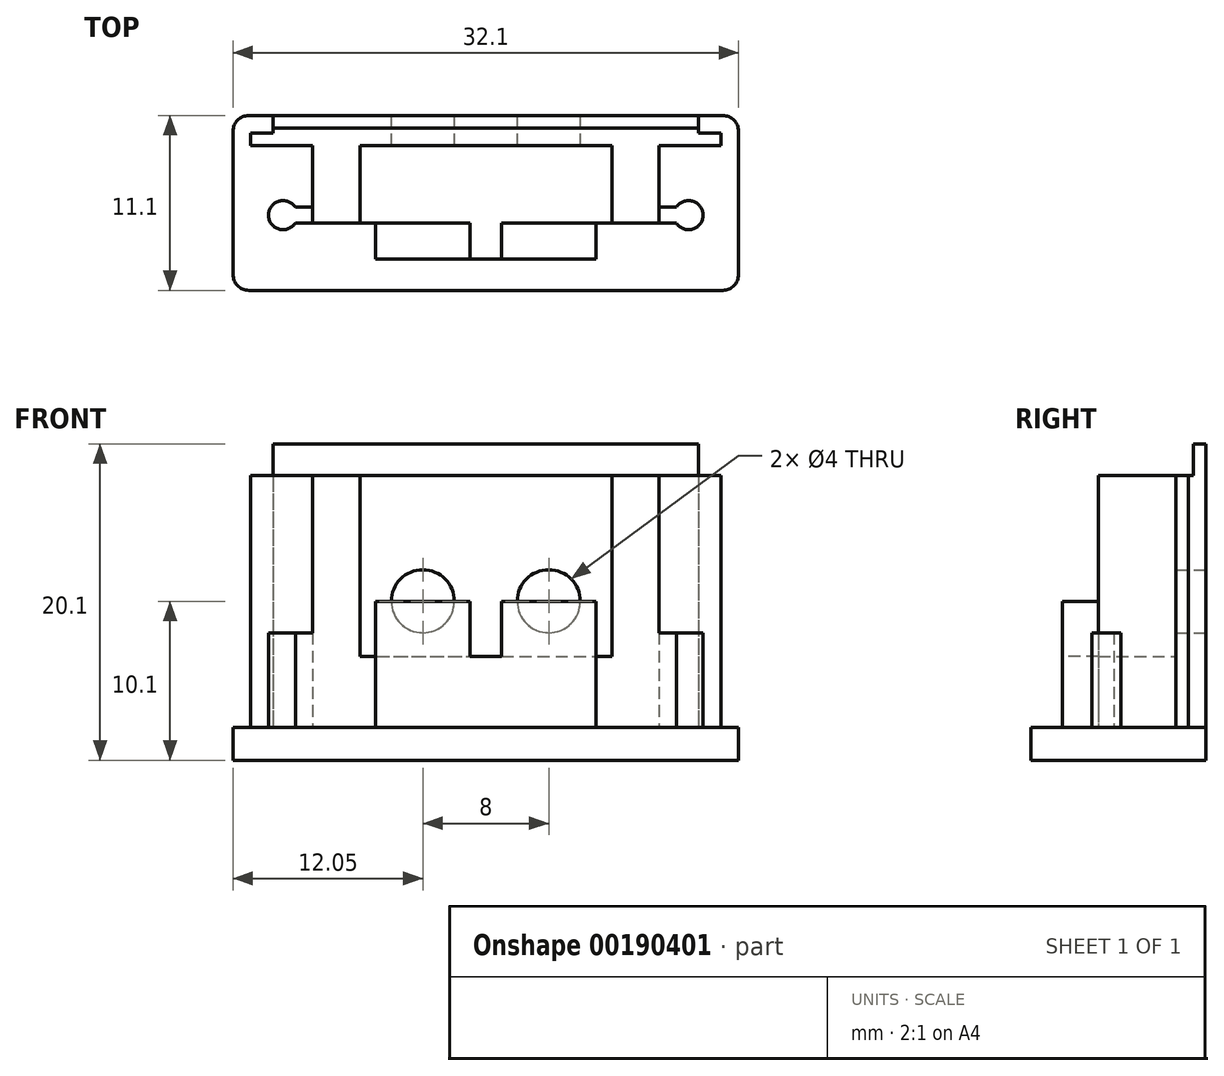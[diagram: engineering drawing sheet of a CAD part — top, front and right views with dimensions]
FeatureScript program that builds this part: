
annotation { "Feature Type Name" : "Feature", "Feature Type Description" : "" }
export const myFeature = defineFeature(function(context is Context, id is Id, definition is map)
    precondition{}
    {
        {
            var Q0;
            Q0=qCreatedBy(makeId("Top.planeOp"),FACE);
            var sketch = newSketch(context, id + "F0", { "sketchPlane" : qUnion([Q0])});
            skLineSegment(sketch, "E0.bottom", {"start": v(-15.05, 5.55) * mm, "end": v(15.05, 5.55) * mm});
            skLineSegment(sketch, "E0.top", {"start": v(-15.05, -5.55) * mm, "end": v(15.05, -5.55) * mm});
            skLineSegment(sketch, "E0.left", {"start": v(-16.05, 4.55) * mm, "end": v(-16.05, -4.55) * mm});
            skLineSegment(sketch, "E0.right", {"start": v(16.05, 4.55) * mm, "end": v(16.05, -4.55) * mm});
            skPoint(sketch, "E1.visualSharp", {"position": v(-16.05, 5.55) * mm});
            skArc(sketch, "E1.filletArc", {"start": v(-15.05, 5.55) * mm, "mid": v(-15.76, 5.26) * mm, "end": v(-16.05, 4.55) * mm});
            skPoint(sketch, "E2.visualSharp", {"position": v(-16.05, -5.55) * mm});
            skArc(sketch, "E2.filletArc", {"start": v(-16.05, -4.55) * mm, "mid": v(-15.76, -5.26) * mm, "end": v(-15.05, -5.55) * mm});
            skPoint(sketch, "E3.visualSharp", {"position": v(16.05, 5.55) * mm});
            skArc(sketch, "E3.filletArc", {"start": v(16.05, 4.55) * mm, "mid": v(15.76, 5.26) * mm, "end": v(15.05, 5.55) * mm});
            skPoint(sketch, "E4.visualSharp", {"position": v(16.05, -5.55) * mm});
            skArc(sketch, "E4.filletArc", {"start": v(15.05, -5.55) * mm, "mid": v(15.76, -5.26) * mm, "end": v(16.05, -4.55) * mm});
            skSolve(sketch);
        }
        {
            var Q0;
            Q0=makeQuery(id+"F0.imprint","IMPRINT",FACE,{"disambiguationData":[TD([[makeQuery(id+"F0.imprint","IMPRINT",EDGE,{"derivedFrom":sQuery(id+"F0.wireOp",EDGE,"E0.bottom")}),-1.0]])]});
            extrude(context, id + "F1", {"entities" : qUnion([Q0]), "depth" : 2.1 * mm});
        }
        {
            var Q0;
            Q0=makeQuery(id+"F1.opExtrude","CAP_FACE",FACE,{"disambiguationData":[OSD([sQuery(id+"F0.wireOp",EDGE,"E0.bottom"),sQuery(id+"F0.wireOp",EDGE,"E0.top"),sQuery(id+"F0.wireOp",EDGE,"E0.left"),sQuery(id+"F0.wireOp",EDGE,"E0.right"),sQuery(id+"F0.wireOp",EDGE,"E1.filletArc"),sQuery(id+"F0.wireOp",EDGE,"E2.filletArc"),sQuery(id+"F0.wireOp",EDGE,"E3.filletArc"),sQuery(id+"F0.wireOp",EDGE,"E4.filletArc")])],"isStart":false});
            var sketch = newSketch(context, id + "F2", { "sketchPlane" : qUnion([Q0])});
            skLineSegment(sketch, "E5.bottom", {"start": v(-13.5, 5.55) * mm, "end": v(13.5, 5.55) * mm});
            skLineSegment(sketch, "E5.top", {"start": v(-13.5, 4.45) * mm, "end": v(13.5, 4.45) * mm});
            skLineSegment(sketch, "E5.left", {"start": v(-13.5, 5.55) * mm, "end": v(-13.5, 4.45) * mm});
            skLineSegment(sketch, "E5.right", {"start": v(13.5, 5.55) * mm, "end": v(13.5, 4.45) * mm});
            skLineSegment(sketch, "E6.bottom", {"start": v(-14.93, 4.45) * mm, "end": v(14.93, 4.45) * mm});
            skLineSegment(sketch, "E6.top", {"start": v(-14.93, 3.65) * mm, "end": v(14.93, 3.65) * mm});
            skLineSegment(sketch, "E6.left", {"start": v(-14.93, 4.45) * mm, "end": v(-14.93, 3.65) * mm});
            skLineSegment(sketch, "E6.right", {"start": v(14.93, 4.45) * mm, "end": v(14.93, 3.65) * mm});
            skCircle(sketch, "E7", {"center": v(-12.88, -0.77) * mm, "radius": 0.93 * mm});
            skCircle(sketch, "E8", {"center": v(12.88, -0.78) * mm, "radius": 0.93 * mm});
            skLineSegment(sketch, "E9.bottom", {"start": v(-12.88, -0.27) * mm, "end": v(12.88, -0.28) * mm});
            skLineSegment(sketch, "E9.top", {"start": v(-12.88, -1.27) * mm, "end": v(12.88, -1.28) * mm});
            skLineSegment(sketch, "E9.left", {"start": v(-12.88, -0.27) * mm, "end": v(-12.88, -1.27) * mm});
            skLineSegment(sketch, "E9.right", {"start": v(12.88, -0.28) * mm, "end": v(12.88, -1.28) * mm});
            skLineSegment(sketch, "E10", {"start": v(-12.88, -0.77) * mm, "end": v(12.88, -0.78) * mm, "construction": true});
            skSolve(sketch);
        }
        {
            var Q0;
            {var subQ5=sQuery(id+"F2.wireOp",EDGE,"E9.right");Q0=makeQuery(id+"F2.imprint","IMPRINT",FACE,{"disambiguationData":[TD([[makeQuery(id+"F2.imprint","IMPRINT",EDGE,{"derivedFrom":subQ5}),1.0]])]});}
            var Q1;
            {var subQ0=sQuery(id+"F2.wireOp",EDGE,"E9.bottom");var subQ1=sQuery(id+"F2.wireOp",EDGE,"E7");var subQ2=makeQuery(id+"F2.imprint","INTERSECT",VERTEX,{"derivedFrom":[subQ1,subQ0]});Q1=makeQuery(id+"F2.imprint","IMPRINT",FACE,{"disambiguationData":[TD([[makeQuery(id+"F2.imprint","IMPRINT",EDGE,{"disambiguationData":[TD([[subQ2,1.0]])],"derivedFrom":subQ1}),-1.0]])]});}
            var Q2;
            {var subQ5=sQuery(id+"F2.wireOp",EDGE,"E9.right");Q2=makeQuery(id+"F2.imprint","IMPRINT",FACE,{"disambiguationData":[TD([[makeQuery(id+"F2.imprint","IMPRINT",EDGE,{"derivedFrom":subQ5}),-1.0]])]});}
            var Q3;
            {var subQ5=sQuery(id+"F2.wireOp",EDGE,"E9.left");Q3=makeQuery(id+"F2.imprint","IMPRINT",FACE,{"disambiguationData":[TD([[makeQuery(id+"F2.imprint","IMPRINT",EDGE,{"derivedFrom":subQ5}),-1.0]])]});}
            var Q4;
            {var subQ5=sQuery(id+"F2.wireOp",EDGE,"E9.left");Q4=makeQuery(id+"F2.imprint","IMPRINT",FACE,{"disambiguationData":[TD([[makeQuery(id+"F2.imprint","IMPRINT",EDGE,{"derivedFrom":subQ5}),1.0]])]});}
            var Q5;
            Q5=makeQuery(id+"F2.imprint","IMPRINT",FACE,{"disambiguationData":[TD([[makeQuery(id+"F2.imprint","IMPRINT",EDGE,{"derivedFrom":sQuery(id+"F2.wireOp",EDGE,"E6.top")}),1.0]])]});
            var Q6;
            Q6=makeQuery(id+"F2.imprint","IMPRINT",FACE,{"disambiguationData":[TD([[makeQuery(id+"F2.imprint","IMPRINT",EDGE,{"derivedFrom":sQuery(id+"F2.wireOp",EDGE,"E5.bottom")}),-1.0]])]});
            extrude(context, id + "F3", {"entities" : qUnion([Q0, Q1, Q2, Q3, Q4, Q5, Q6]), "operationType" : NewBodyOperationType.ADD, "depth" : 4.5 * mm});
        }
        {
            var Q0;
            Q0=makeQuery(id+"F3.opExtrude","CAP_FACE",FACE,{"disambiguationData":[OSD([sQuery(id+"F2.wireOp",EDGE,"E5.bottom"),sQuery(id+"F2.wireOp",EDGE,"E5.left"),sQuery(id+"F2.wireOp",EDGE,"E5.right"),sQuery(id+"F2.wireOp",EDGE,"E6.bottom"),sQuery(id+"F2.wireOp",EDGE,"E6.top"),sQuery(id+"F2.wireOp",EDGE,"E6.left"),sQuery(id+"F2.wireOp",EDGE,"E6.right")])],"isStart":false});
            extrude(context, id + "F4", {"entities" : qUnion([Q0]), "operationType" : NewBodyOperationType.ADD, "depth" : (10 + 1.5) * mm});
        }
        {
            var Q0;
            {var subQ0=sQuery(id+"F2.wireOp",EDGE,"E5.bottom");Q0=makeQuery(id+"F4.boolean.opBoolean","MERGE",FACE,{"derivedFrom":[makeQuery(id+"F3.boolean.opBoolean","MERGE",FACE,{"derivedFrom":[makeQuery(id+"F1.opExtrude","SWEPT_FACE",FACE,{"disambiguationData":[OSD([sQuery(id+"F0.wireOp",EDGE,"E0.bottom")])]}),makeQuery(id+"F3.opExtrude","SWEPT_FACE",FACE,{"disambiguationData":[OSD([subQ0])]})]}),makeQuery(id+"F4.opExtrude","SWEPT_FACE",FACE,{"disambiguationData":[OSD([subQ0])]})]});}
            var sketch = newSketch(context, id + "F5", { "sketchPlane" : qUnion([Q0])});
            skCircle(sketch, "E11", {"center": v(-4, 10.1) * mm, "radius": 2 * mm});
            skCircle(sketch, "E12", {"center": v(4, 10.1) * mm, "radius": 2 * mm});
            skSolve(sketch);
        }
        {
            var Q0;
            Q0=makeQuery(id+"F5.imprint","IMPRINT",FACE,{"disambiguationData":[TD([[makeQuery(id+"F5.imprint","IMPRINT",EDGE,{"derivedFrom":sQuery(id+"F5.wireOp",EDGE,"E12")}),1.0]])]});
            var Q1;
            Q1=makeQuery(id+"F5.imprint","IMPRINT",FACE,{"disambiguationData":[TD([[makeQuery(id+"F5.imprint","IMPRINT",EDGE,{"derivedFrom":sQuery(id+"F5.wireOp",EDGE,"E11")}),1.0]])]});
            extrude(context, id + "F6", {"entities" : qUnion([Q0, Q1]), "operationType" : NewBodyOperationType.REMOVE, "oppositeDirection" : true, "depth" : 25 * mm});
        }
        {
            var Q0;
            Q0=makeQuery(id+"F1.opExtrude","CAP_FACE",FACE,{"disambiguationData":[OSD([sQuery(id+"F0.wireOp",EDGE,"E0.bottom"),sQuery(id+"F0.wireOp",EDGE,"E0.top"),sQuery(id+"F0.wireOp",EDGE,"E0.left"),sQuery(id+"F0.wireOp",EDGE,"E0.right"),sQuery(id+"F0.wireOp",EDGE,"E1.filletArc"),sQuery(id+"F0.wireOp",EDGE,"E2.filletArc"),sQuery(id+"F0.wireOp",EDGE,"E3.filletArc"),sQuery(id+"F0.wireOp",EDGE,"E4.filletArc")])],"isStart":false});
            var sketch = newSketch(context, id + "F7", { "sketchPlane" : qUnion([Q0])});
            skLineSegment(sketch, "E13.bottom", {"start": v(-11, -0.27) * mm, "end": v(11, -0.27) * mm});
            skLineSegment(sketch, "E13.top", {"start": v(-11, 3.65) * mm, "end": v(11, 3.65) * mm});
            skLineSegment(sketch, "E13.left", {"start": v(-11, -0.28) * mm, "end": v(-11, 3.65) * mm});
            skLineSegment(sketch, "E13.right", {"start": v(11, -0.28) * mm, "end": v(11, 3.65) * mm});
            skSolve(sketch);
        }
        {
            var Q0;
            Q0=makeQuery(id+"F7.imprint","IMPRINT",FACE,{"disambiguationData":[TD([[makeQuery(id+"F7.imprint","IMPRINT",EDGE,{"derivedFrom":sQuery(id+"F7.wireOp",EDGE,"E13.bottom")}),1.0]])]});
            var Q1;
            Q1=makeQuery(id+"F3.opExtrude","CAP_FACE",FACE,{"disambiguationData":[OSD([sQuery(id+"F2.wireOp",EDGE,"E7"),sQuery(id+"F2.wireOp",EDGE,"E8"),sQuery(id+"F2.wireOp",EDGE,"E9.bottom"),sQuery(id+"F2.wireOp",EDGE,"E9.top")])],"isStart":false});
            extrude(context, id + "F8", {"entities" : qUnion([Q0]), "operationType" : NewBodyOperationType.ADD, "endBound" : BoundingType.UP_TO_SURFACE, "endBoundEntityFace" : qUnion([Q1]), "depth" : 25 * mm});
        }
        {
            var Q0;
            Q0=makeQuery(id+"F8.boolean.opBoolean","MERGE",FACE,{"derivedFrom":[makeQuery(id+"F3.opExtrude","CAP_FACE",FACE,{"disambiguationData":[OSD([sQuery(id+"F2.wireOp",EDGE,"E7"),sQuery(id+"F2.wireOp",EDGE,"E8"),sQuery(id+"F2.wireOp",EDGE,"E9.bottom"),sQuery(id+"F2.wireOp",EDGE,"E9.top")])],"isStart":false}),makeQuery(id+"F8.opExtrude","CAP_FACE",FACE,{"disambiguationData":[OSD([sQuery(id+"F7.wireOp",EDGE,"E13.bottom"),sQuery(id+"F7.wireOp",EDGE,"E13.top"),sQuery(id+"F7.wireOp",EDGE,"E13.left"),sQuery(id+"F7.wireOp",EDGE,"E13.right")])],"isStart":false})]});
            var sketch = newSketch(context, id + "F9", { "sketchPlane" : qUnion([Q0])});
            skArc(sketch, "E14.0.0", {"start": v(-12.1, -0.27) * mm, "mid": v(-13.8, -0.77) * mm, "end": v(-12.1, -1.27) * mm});
            skLineSegment(sketch, "E14.0.1", {"start": v(-12.1, -1.27) * mm, "end": v(12.1, -1.28) * mm});
            skArc(sketch, "E14.0.2", {"start": v(12.1, -1.28) * mm, "mid": v(13.8, -0.78) * mm, "end": v(12.1, -0.28) * mm});
            skLineSegment(sketch, "E14.0.3", {"start": v(12.1, -0.28) * mm, "end": v(11, -0.28) * mm});
            skLineSegment(sketch, "E14.0.4", {"start": v(11, -0.28) * mm, "end": v(11, 3.65) * mm});
            skLineSegment(sketch, "E14.0.5", {"start": v(11, 3.65) * mm, "end": v(-11, 3.65) * mm});
            skLineSegment(sketch, "E14.0.6", {"start": v(-11, 3.65) * mm, "end": v(-11, -0.27) * mm});
            skLineSegment(sketch, "E14.0.7", {"start": v(-11, -0.27) * mm, "end": v(-12.1, -0.27) * mm});
            skLineSegment(sketch, "E15", {"start": v(-8, -1.28) * mm, "end": v(-8, 3.65) * mm});
            skLineSegment(sketch, "E16", {"start": v(8, -1.28) * mm, "end": v(8, 3.65) * mm});
            skSolve(sketch);
        }
        {
            var Q0;
            {var subQ4=sQuery(id+"F9.wireOp",EDGE,"E14.0.0");Q0=makeQuery(id+"F9.imprint","IMPRINT",FACE,{"disambiguationData":[TD([[makeQuery(id+"F9.imprint","IMPRINT",EDGE,{"derivedFrom":subQ4}),1.0]])]});}
            var Q1;
            {var subQ1=sQuery(id+"F9.wireOp",EDGE,"E14.0.2");Q1=makeQuery(id+"F9.imprint","IMPRINT",FACE,{"disambiguationData":[TD([[makeQuery(id+"F9.imprint","IMPRINT",EDGE,{"derivedFrom":subQ1}),1.0]])]});}
            var Q2;
            Q2=makeQuery(id+"F4.opExtrude","CAP_FACE",FACE,{"disambiguationData":[OSD([sQuery(id+"F2.wireOp",EDGE,"E5.bottom"),sQuery(id+"F2.wireOp",EDGE,"E5.left"),sQuery(id+"F2.wireOp",EDGE,"E5.right"),sQuery(id+"F2.wireOp",EDGE,"E6.bottom"),sQuery(id+"F2.wireOp",EDGE,"E6.top"),sQuery(id+"F2.wireOp",EDGE,"E6.left"),sQuery(id+"F2.wireOp",EDGE,"E6.right")])],"isStart":false});
            extrude(context, id + "F10", {"entities" : qUnion([Q0, Q1]), "operationType" : NewBodyOperationType.ADD, "endBound" : BoundingType.UP_TO_SURFACE, "endBoundEntityFace" : qUnion([Q2]), "depth" : 25 * mm});
        }
        {
            var Q0;
            Q0=makeQuery(id+"F1.opExtrude","CAP_FACE",FACE,{"disambiguationData":[OSD([sQuery(id+"F0.wireOp",EDGE,"E0.bottom"),sQuery(id+"F0.wireOp",EDGE,"E0.top"),sQuery(id+"F0.wireOp",EDGE,"E0.left"),sQuery(id+"F0.wireOp",EDGE,"E0.right"),sQuery(id+"F0.wireOp",EDGE,"E1.filletArc"),sQuery(id+"F0.wireOp",EDGE,"E2.filletArc"),sQuery(id+"F0.wireOp",EDGE,"E3.filletArc"),sQuery(id+"F0.wireOp",EDGE,"E4.filletArc")])],"isStart":false});
            var sketch = newSketch(context, id + "F11", { "sketchPlane" : qUnion([Q0])});
            skLineSegment(sketch, "E17.bottom", {"start": v(-7, -1.28) * mm, "end": v(-1, -1.28) * mm});
            skLineSegment(sketch, "E17.top", {"start": v(-7, -3.55) * mm, "end": v(-1, -3.55) * mm});
            skLineSegment(sketch, "E17.left", {"start": v(-7, -1.28) * mm, "end": v(-7, -3.55) * mm});
            skLineSegment(sketch, "E17.right", {"start": v(-1, -1.28) * mm, "end": v(-1, -3.55) * mm});
            skLineSegment(sketch, "E18.MirrorCS", {"start": v(1, -1.28) * mm, "end": v(1, -3.55) * mm});
            skLineSegment(sketch, "E19.MirrorCS", {"start": v(7, -3.55) * mm, "end": v(1, -3.55) * mm});
            skLineSegment(sketch, "E20.MirrorCS", {"start": v(7, -1.28) * mm, "end": v(7, -3.55) * mm});
            skLineSegment(sketch, "E21.MirrorCS", {"start": v(7, -1.28) * mm, "end": v(1, -1.28) * mm});
            skSolve(sketch);
        }
        {
            var Q0;
            Q0=makeQuery(id+"F11.imprint","IMPRINT",FACE,{"disambiguationData":[TD([[makeQuery(id+"F11.imprint","IMPRINT",EDGE,{"derivedFrom":sQuery(id+"F11.wireOp",EDGE,"E17.bottom")}),-1.0]])]});
            var Q1;
            Q1=makeQuery(id+"F11.imprint","IMPRINT",FACE,{"disambiguationData":[TD([[makeQuery(id+"F11.imprint","IMPRINT",EDGE,{"derivedFrom":sQuery(id+"F11.wireOp",EDGE,"E18.MirrorCS")}),1.0]])]});
            extrude(context, id + "F12", {"entities" : qUnion([Q0, Q1]), "operationType" : NewBodyOperationType.ADD, "depth" : 8 * mm});
        }
        {
            var Q0;
            {var subQ0=sQuery(id+"F9.wireOp",EDGE,"E14.0.5");var subQ1=sQuery(id+"F9.wireOp",EDGE,"E14.0.1");Q0=makeQuery(id+"F10.boolean.opBoolean","MERGE",FACE,{"derivedFrom":[makeQuery(id+"F4.opExtrude","CAP_FACE",FACE,{"disambiguationData":[OSD([sQuery(id+"F2.wireOp",EDGE,"E5.bottom"),sQuery(id+"F2.wireOp",EDGE,"E5.left"),sQuery(id+"F2.wireOp",EDGE,"E5.right"),sQuery(id+"F2.wireOp",EDGE,"E6.bottom"),sQuery(id+"F2.wireOp",EDGE,"E6.top"),sQuery(id+"F2.wireOp",EDGE,"E6.left"),sQuery(id+"F2.wireOp",EDGE,"E6.right")])],"isStart":false}),makeQuery(id+"F10.opExtrude","CAP_FACE",FACE,{"disambiguationData":[OSD([sQuery(id+"F9.wireOp",EDGE,"E14.0.0"),subQ1,subQ0,sQuery(id+"F9.wireOp",EDGE,"E14.0.6"),sQuery(id+"F9.wireOp",EDGE,"E14.0.7"),sQuery(id+"F9.wireOp",EDGE,"E15")])],"isStart":false}),makeQuery(id+"F10.opExtrude","CAP_FACE",FACE,{"disambiguationData":[OSD([subQ1,sQuery(id+"F9.wireOp",EDGE,"E14.0.2"),sQuery(id+"F9.wireOp",EDGE,"E14.0.3"),sQuery(id+"F9.wireOp",EDGE,"E14.0.4"),subQ0,sQuery(id+"F9.wireOp",EDGE,"E16")])],"isStart":false})]});}
            var sketch = newSketch(context, id + "F13", { "sketchPlane" : qUnion([Q0])});
            skLineSegment(sketch, "E22.bottom", {"start": v(-13.5, 5.55) * mm, "end": v(13.5, 5.55) * mm});
            skLineSegment(sketch, "E22.left", {"start": v(-13.5, 5.55) * mm, "end": v(-13.5, 4.75) * mm});
            skLineSegment(sketch, "E22.right", {"start": v(13.5, 5.55) * mm, "end": v(13.5, 4.75) * mm});
            skLineSegment(sketch, "E23", {"start": v(-13.5, 4.75) * mm, "end": v(13.5, 4.75) * mm});
            skSolve(sketch);
        }
        {
            var Q0;
            Q0=makeQuery(id+"F13.imprint","IMPRINT",FACE,{"disambiguationData":[TD([[makeQuery(id+"F13.imprint","IMPRINT",EDGE,{"derivedFrom":sQuery(id+"F13.wireOp",EDGE,"E22.bottom")}),-1.0]])]});
            extrude(context, id + "F14", {"entities" : qUnion([Q0]), "operationType" : NewBodyOperationType.ADD, "depth" : 2 * mm});
        }
        {
            var Q0;
            Q0=makeQuery(id+"F1.opExtrude","CAP_FACE",FACE,{"disambiguationData":[OSD([sQuery(id+"F0.wireOp",EDGE,"E0.bottom"),sQuery(id+"F0.wireOp",EDGE,"E0.top"),sQuery(id+"F0.wireOp",EDGE,"E0.left"),sQuery(id+"F0.wireOp",EDGE,"E0.right"),sQuery(id+"F0.wireOp",EDGE,"E1.filletArc"),sQuery(id+"F0.wireOp",EDGE,"E2.filletArc"),sQuery(id+"F0.wireOp",EDGE,"E3.filletArc"),sQuery(id+"F0.wireOp",EDGE,"E4.filletArc")])],"isStart":false});
            var sketch = newSketch(context, id + "F15", { "sketchPlane" : qUnion([Q0])});
            skLineSegment(sketch, "E24.bottom", {"start": v(-1, -1.28) * mm, "end": v(1, -1.28) * mm});
            skLineSegment(sketch, "E24.top", {"start": v(-1, -3.55) * mm, "end": v(1, -3.55) * mm});
            skLineSegment(sketch, "E24.left", {"start": v(-1, -1.28) * mm, "end": v(-1, -3.55) * mm});
            skLineSegment(sketch, "E24.right", {"start": v(1, -1.28) * mm, "end": v(1, -3.55) * mm});
            skSolve(sketch);
        }
        {
            var Q0;
            Q0=makeQuery(id+"F15.imprint","IMPRINT",FACE,{"disambiguationData":[TD([[makeQuery(id+"F15.imprint","IMPRINT",EDGE,{"derivedFrom":sQuery(id+"F15.wireOp",EDGE,"E24.bottom")}),-1.0]])]});
            var Q1;
            Q1=makeQuery(id+"F8.boolean.opBoolean","MERGE",FACE,{"derivedFrom":[makeQuery(id+"F3.opExtrude","CAP_FACE",FACE,{"disambiguationData":[OSD([sQuery(id+"F2.wireOp",EDGE,"E7"),sQuery(id+"F2.wireOp",EDGE,"E8"),sQuery(id+"F2.wireOp",EDGE,"E9.bottom"),sQuery(id+"F2.wireOp",EDGE,"E9.top")])],"isStart":false}),makeQuery(id+"F8.opExtrude","CAP_FACE",FACE,{"disambiguationData":[OSD([sQuery(id+"F7.wireOp",EDGE,"E13.bottom"),sQuery(id+"F7.wireOp",EDGE,"E13.top"),sQuery(id+"F7.wireOp",EDGE,"E13.left"),sQuery(id+"F7.wireOp",EDGE,"E13.right")])],"isStart":false})]});
            extrude(context, id + "F16", {"entities" : qUnion([Q0]), "operationType" : NewBodyOperationType.ADD, "endBound" : BoundingType.UP_TO_SURFACE, "endBoundEntityFace" : qUnion([Q1]), "depth" : 25 * mm});
        }
        {
            var Q0;
            {var subQ0=sQuery(id+"F9.wireOp",EDGE,"E14.0.5");var subQ1=sQuery(id+"F9.wireOp",EDGE,"E14.0.1");Q0=makeQuery(id+"F10.boolean.opBoolean","MERGE",FACE,{"derivedFrom":[makeQuery(id+"F4.opExtrude","CAP_FACE",FACE,{"disambiguationData":[OSD([sQuery(id+"F2.wireOp",EDGE,"E5.bottom"),sQuery(id+"F2.wireOp",EDGE,"E5.left"),sQuery(id+"F2.wireOp",EDGE,"E5.right"),sQuery(id+"F2.wireOp",EDGE,"E6.bottom"),sQuery(id+"F2.wireOp",EDGE,"E6.top"),sQuery(id+"F2.wireOp",EDGE,"E6.left"),sQuery(id+"F2.wireOp",EDGE,"E6.right")])],"isStart":false}),makeQuery(id+"F10.opExtrude","CAP_FACE",FACE,{"disambiguationData":[OSD([sQuery(id+"F9.wireOp",EDGE,"E14.0.0"),subQ1,subQ0,sQuery(id+"F9.wireOp",EDGE,"E14.0.6"),sQuery(id+"F9.wireOp",EDGE,"E14.0.7"),sQuery(id+"F9.wireOp",EDGE,"E15")])],"isStart":false}),makeQuery(id+"F10.opExtrude","CAP_FACE",FACE,{"disambiguationData":[OSD([subQ1,sQuery(id+"F9.wireOp",EDGE,"E14.0.2"),sQuery(id+"F9.wireOp",EDGE,"E14.0.3"),sQuery(id+"F9.wireOp",EDGE,"E14.0.4"),subQ0,sQuery(id+"F9.wireOp",EDGE,"E16")])],"isStart":false})]});}
            var sketch = newSketch(context, id + "F17", { "sketchPlane" : qUnion([Q0])});
            skLineSegment(sketch, "E25.0.0", {"start": v(13.5, 4.75) * mm, "end": v(-13.5, 4.75) * mm});
            skLineSegment(sketch, "E25.0.1", {"start": v(-13.5, 4.75) * mm, "end": v(-13.5, 4.45) * mm});
            skLineSegment(sketch, "E25.0.2", {"start": v(-13.5, 4.45) * mm, "end": v(-14.93, 4.45) * mm});
            skLineSegment(sketch, "E25.0.3", {"start": v(-14.93, 4.45) * mm, "end": v(-14.93, 3.65) * mm});
            skLineSegment(sketch, "E25.0.4", {"start": v(-14.93, 3.65) * mm, "end": v(-11, 3.65) * mm});
            skLineSegment(sketch, "E25.0.5", {"start": v(-11, 3.65) * mm, "end": v(-11, -0.27) * mm});
            skLineSegment(sketch, "E25.0.6", {"start": v(-11, -0.27) * mm, "end": v(-12.1, -0.27) * mm});
            skArc(sketch, "E25.0.7", {"start": v(-12.1, -0.27) * mm, "mid": v(-13.8, -0.77) * mm, "end": v(-12.1, -1.27) * mm});
            skLineSegment(sketch, "E25.0.8", {"start": v(-12.1, -1.27) * mm, "end": v(-8, -1.28) * mm});
            skLineSegment(sketch, "E25.0.9", {"start": v(-8, -1.28) * mm, "end": v(-8, 3.65) * mm});
            skLineSegment(sketch, "E25.0.10", {"start": v(-8, 3.65) * mm, "end": v(8, 3.65) * mm});
            skLineSegment(sketch, "E25.0.11", {"start": v(8, 3.65) * mm, "end": v(8, -1.28) * mm});
            skLineSegment(sketch, "E25.0.12", {"start": v(8, -1.28) * mm, "end": v(12.1, -1.28) * mm});
            skArc(sketch, "E25.0.13", {"start": v(12.1, -1.28) * mm, "mid": v(13.8, -0.78) * mm, "end": v(12.1, -0.28) * mm});
            skLineSegment(sketch, "E25.0.14", {"start": v(12.1, -0.28) * mm, "end": v(11, -0.28) * mm});
            skLineSegment(sketch, "E25.0.15", {"start": v(11, -0.28) * mm, "end": v(11, 3.65) * mm});
            skLineSegment(sketch, "E25.0.16", {"start": v(11, 3.65) * mm, "end": v(14.93, 3.65) * mm});
            skLineSegment(sketch, "E25.0.17", {"start": v(14.93, 3.65) * mm, "end": v(14.93, 4.45) * mm});
            skLineSegment(sketch, "E25.0.18", {"start": v(14.93, 4.45) * mm, "end": v(13.5, 4.45) * mm});
            skLineSegment(sketch, "E25.0.19", {"start": v(13.5, 4.45) * mm, "end": v(13.5, 4.75) * mm});
            skLineSegment(sketch, "E26", {"start": v(-11, -0.27) * mm, "end": v(-11, -1.27) * mm});
            skLineSegment(sketch, "E27", {"start": v(11, -0.28) * mm, "end": v(11, -1.28) * mm});
            skSolve(sketch);
        }
        {
            var Q0;
            Q0=makeQuery(id+"F17.imprint","IMPRINT",FACE,{"disambiguationData":[TD([[makeQuery(id+"F17.imprint","IMPRINT",EDGE,{"derivedFrom":sQuery(id+"F17.wireOp",EDGE,"E25.0.6")}),-1.0]])]});
            var Q1;
            {var subQ0=sQuery(id+"F17.wireOp",EDGE,"E25.0.13");Q1=makeQuery(id+"F17.imprint","IMPRINT",FACE,{"disambiguationData":[TD([[makeQuery(id+"F17.imprint","IMPRINT",EDGE,{"derivedFrom":subQ0}),1.0]])]});}
            extrude(context, id + "F18", {"entities" : qUnion([Q0, Q1]), "operationType" : NewBodyOperationType.REMOVE, "oppositeDirection" : true, "depth" : 10 * mm});
        }
    });
